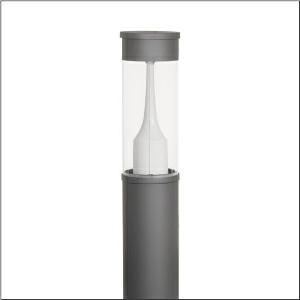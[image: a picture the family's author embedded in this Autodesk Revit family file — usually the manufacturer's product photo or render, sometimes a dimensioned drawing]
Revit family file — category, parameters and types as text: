
# Revit family: city-light_400_iq___p1_0a_5xa5305nf14h_7630
name_source: partatom
category: Lighting Fixtures
units: mm (PartAtom-declared; Revit-internal decimal feet)

## family parameters
Cut with Voids When Loaded = No
Host = Face
Light Source = No
Part Type = Normal
Room Calculation Point = No
Round Connector Dimension = Use Diameter
Shared = No

## types (1)
- --- (1 x LED, 1510 lm, 11.8 W, 2700K)
    Apparent Load = 12 VA
    CIE Flux Codes = 32 61 90 93 100
    Color Rendering = 70
    Color Temperature = 2700K
    Default Elevation = 1800 mm
    Description = City-Light 400 iQ, light pillar, Module 540 iQ-SR, primary light control with 3 zone facetted reflector, of plastic, silver coated, highly specular, structured, primary optical cover: cover, of PMMA, transparent, partly coated, light distribution: P1.0a, primary light characteristic: strongly asymmetric, LED, High Power LED, rated luminous flux: 1.510lm, luminous efficacy: 128lm/W, light colour: 727, colour temperature: 2700K, control gear: ECG iQ, control: presetting dimming logarithmic, Street-Remote, Auto-Match, Temp-Guard, Lumen-Switch, Night-Set, Smart-Wire, Light-Fading, Desk-Remote (wireless, voltage-free reading and setting of iQ features in the workshop via application-optimized NFC function/RFID function), optimised constant luminous flux control (CLO 2.0), with terminal, 6-pole, max. 2.5mm², mains connection: 230..240V, AC, 50/60Hz, start of lifetime: 12W, end of service life: 12W, reduction: 6W, luminaire housing, cylindrical, of extruded aluminium section, coated, Siteco® metallic grey (DB 702S), length: 4.694mm, diameter: 200mm, Module 540 iQ-SR, traffic white (RAL 9016), equipment: standard, protection rating (complete): IP65, insulation class (complete): insulation class II (safety insulation), certification: CE, ENEC, VDE, packaging unit: 1 piece

Light Distribution: P1.0a
    Height = 500 mm
    Lamp = 1 x LED
    Lamp Light Flux = 1510 lm
    Lamp Power = 11.8 W
    Lamp count = 1
    Length = 200 mm  [stored 0.656168 ft]
    Luminous efficacy = 128 lm/W
    Manufacturer = Siteco
    ModVariant = No
    Model = 5XA5305NF14H
    Mounting Place = Floor
    Mounting Type = Freestanding
    Number of Poles = 1
    OnlyDefault = Yes
    Power Factor = 1
    Product Name = City-Light 400 iQ | P1.0a
    Product group = light pillar
    ProductGroupID = 1303
    Protection Class = Protection class II
    Protection Degree = IP 65
    RLX_Detail_Level = 1
    RLX_Emergency_Light_Flux = 0 lm
    RLX_Emergency_Type = 0
    RLX_Emergency_Type_DB = No
    RlxData = <blob elided: 75005 chars, md5=96893d00>
    Socket = socket
    Standby Power = 0 W
    System Light Flux = 1510 lm
    System Power = 12 W
    Type Comments = factory setting: luminous flux: 100 % | dim-lin: 254 | 472 mA
    Type Image = l_1006914.jpg
    URL = http://relux.com
    VarID = @adj_103275
    Voltage = 0 V
    Weight = 0.00 kg
    Width = 0 mm  [stored 0 ft]

note: [stored X ft] marks values corroborated as IEEE doubles in the binary element streams (Revit-internal decimal feet)

## geometry (parser evidence)
native form markers: Blend x4, Sweep x10
no freeform markers — native parametric forms only
